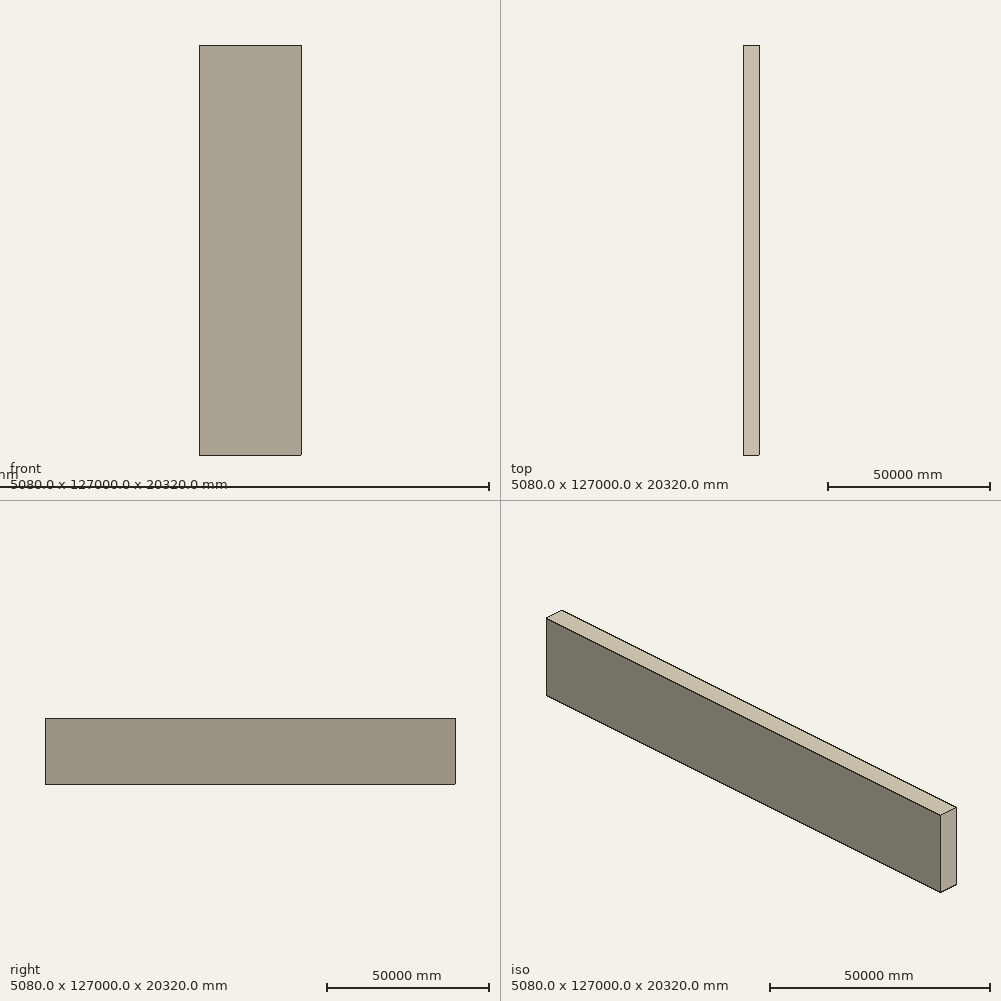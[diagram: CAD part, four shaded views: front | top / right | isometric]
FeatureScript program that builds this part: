
annotation { "Feature Type Name" : "Feature", "Feature Type Description" : "" }
export const myFeature = defineFeature(function(context is Context, id is Id, definition is map)
    precondition{}
    {
        {
            var Q0;
            Q0=qCreatedBy(makeId("Top.planeOp"),FACE);
            var sketch = newSketch(context, id + "F0", { "sketchPlane" : qUnion([Q0])});
            skLineSegment(sketch, "E0", {"start": v(-108, 126994.1) * mm, "end": v(-108, -5.9) * mm});
            skLineSegment(sketch, "E1", {"start": v(-108, -5.9) * mm, "end": v(4972, -5.9) * mm});
            skLineSegment(sketch, "E2", {"start": v(4972, -5.9) * mm, "end": v(4972, 126994.1) * mm});
            skLineSegment(sketch, "E3", {"start": v(4972, 126994.1) * mm, "end": v(-108, 126994.1) * mm});
            skSolve(sketch);
        }
        {
            var Q0;
            Q0=makeQuery(id+"F0.imprint","IMPRINT",FACE,{"disambiguationData":[TD([[makeQuery(id+"F0.imprint","IMPRINT",EDGE,{"derivedFrom":sQuery(id+"F0.wireOp",EDGE,"E0")}),1.0]])]});
            extrude(context, id + "F1", {"entities" : qUnion([Q0]), "depth" : 20320 * mm});
        }
    });
